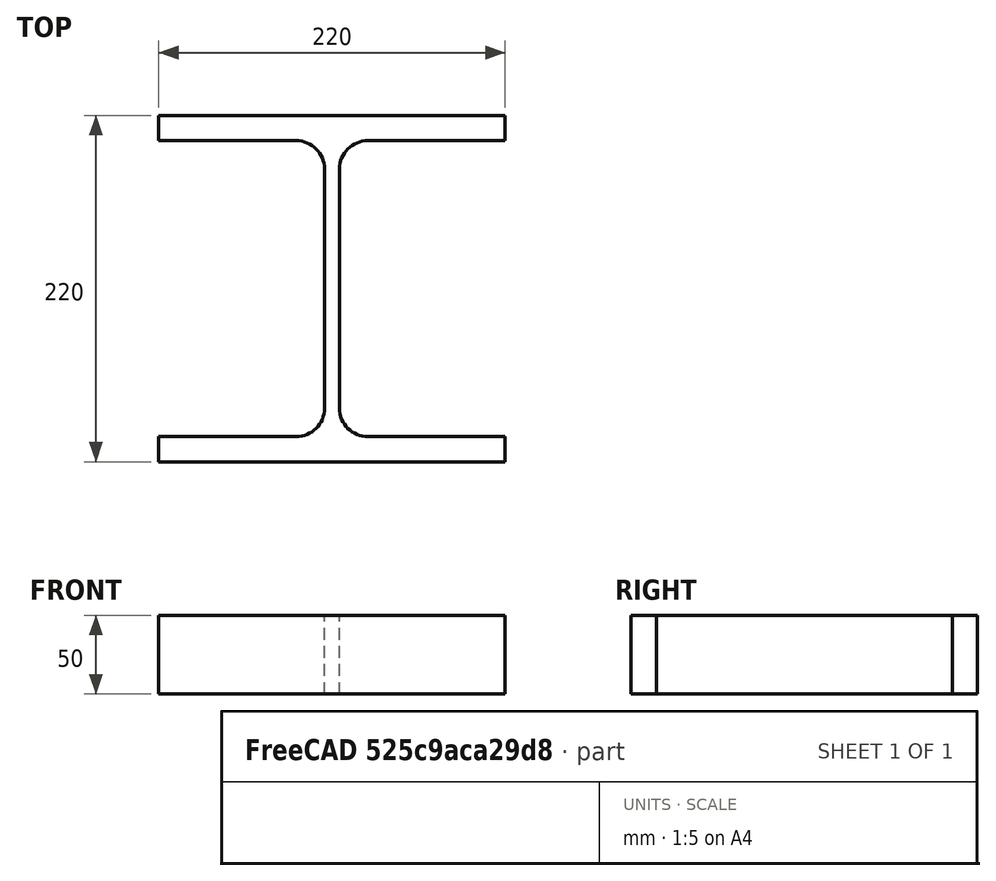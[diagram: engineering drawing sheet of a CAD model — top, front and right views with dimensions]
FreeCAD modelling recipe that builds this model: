
FCSTD DOCUMENT  (FreeCAD 0.15R4671 (Git))
Label: HE-B-Profile 220 DIN1025-2 S235JR
License: All rights reserved
LicenseURL: http://en.wikipedia.org/wiki/All_rights_reserved
objects: Sketcher::SketchObject×1, Part::Extrusion×1
note: 2 computed .brp shape members not serialized (recipe doc carries the construction recipe); baked Part::Feature solids carry a one-line shape summary decoded from their .brp

FEATURE [Sketcher::SketchObject] Sketch
  sketch-geometry (16):
    g0: LineSegment StartX=4.75 StartY=-76 StartZ=0 EndX=4.75 EndY=76 EndZ=0
    g1: LineSegment StartX=22.75 StartY=94 StartZ=0 EndX=110 EndY=94 EndZ=0
    g2: LineSegment StartX=110 StartY=94 StartZ=0 EndX=110 EndY=110 EndZ=0
    g3: LineSegment StartX=110 StartY=110 StartZ=0 EndX=-110 EndY=110 EndZ=0
    g4: LineSegment StartX=-110 StartY=110 StartZ=0 EndX=-110 EndY=94 EndZ=0
    g5: LineSegment StartX=-110 StartY=94 StartZ=0 EndX=-22.75 EndY=94 EndZ=0
    g6: LineSegment StartX=-4.75 StartY=76 StartZ=0 EndX=-4.75 EndY=-76 EndZ=0
    g7: LineSegment StartX=-22.75 StartY=-94 StartZ=0 EndX=-110 EndY=-94 EndZ=0
    g8: LineSegment StartX=-110 StartY=-94 StartZ=0 EndX=-110 EndY=-110 EndZ=0
    g9: LineSegment StartX=-110 StartY=-110 StartZ=0 EndX=110 EndY=-110 EndZ=0
    g10: LineSegment StartX=110 StartY=-110 StartZ=0 EndX=110 EndY=-94 EndZ=0
    g11: LineSegment StartX=110 StartY=-94 StartZ=0 EndX=22.75 EndY=-94 EndZ=0
    g12: ArcOfCircle CenterX=22.75 CenterY=76 CenterZ=0 NormalX=0 NormalY=0 NormalZ=1 Radius=18 StartAngle=1.5708 EndAngle=3.14159
    g13: ArcOfCircle CenterX=22.75 CenterY=-76 CenterZ=0 NormalX=0 NormalY=0 NormalZ=1 Radius=18 StartAngle=3.14159 EndAngle=4.71239
    g14: ArcOfCircle CenterX=-22.75 CenterY=76 CenterZ=0 NormalX=0 NormalY=0 NormalZ=1 Radius=18 StartAngle=0 EndAngle=1.5708
    g15: ArcOfCircle CenterX=-22.75 CenterY=-76 CenterZ=0 NormalX=0 NormalY=0 NormalZ=1 Radius=18 StartAngle=4.71239 EndAngle=6.28319
  constraints (42):
    c: Vertical(g0)
    c: Coincident(g2,g1)
    c: Vertical(g2)
    c: Coincident(g3,g2)
    c: Coincident(g4,g3)
    c: Vertical(g4)
    c: Coincident(g5,g4)
    c: Horizontal(g5)
    c: Vertical(g6)
    c: Horizontal(g7)
    c: Coincident(g8,g7)
    c: Vertical(g8)
    c: Coincident(g9,g8)
    c: Horizontal(g9)
    c: Coincident(g10,g9)
    c: Vertical(g10)
    c: Coincident(g11,g10)
    c: Horizontal(g11)
    c: Tangent(g1,g12) = 1.5708
    c: Tangent(g0,g12) = 1.5708
    c: Tangent(g0,g13) = 1.5708
    c: Tangent(g11,g13) = 1.5708
    c: Tangent(g5,g14) = 1.5708
    c: Tangent(g6,g14) = 1.5708
    c: Tangent(g6,g15) = 1.5708
    c: Tangent(g7,g15) = 1.5708
    c: Equal(g3,g9)
    c: Equal(g2,g4)
    c: Equal(g4,g8)
    c: Equal(g8,g10)
    c: Equal(g12,g14)
    c: Equal(g14,g15)
    c: Equal(g15,g13)
    c: Symmetric(g2,g3,g-2)
    c: Symmetric(g9,g8,g-2)
    c: Symmetric(g0,g6,g-2)
    c: Symmetric(g2,g9,g-1)
    c: DistanceY(g2,g9) = -220
    c: DistanceX(g3) = -220
    c: DistanceX(g0,g6) = -9.5
    c: DistanceY(g2) = 16
    c: Radius(g12) = 18
FEATURE [Part::Extrusion] Extrude  label="HE-B-Profile 220 DIN1025-2 S235JR"
  Base = -> Sketch
  Dir = (0,0,50)
  Solid = true
